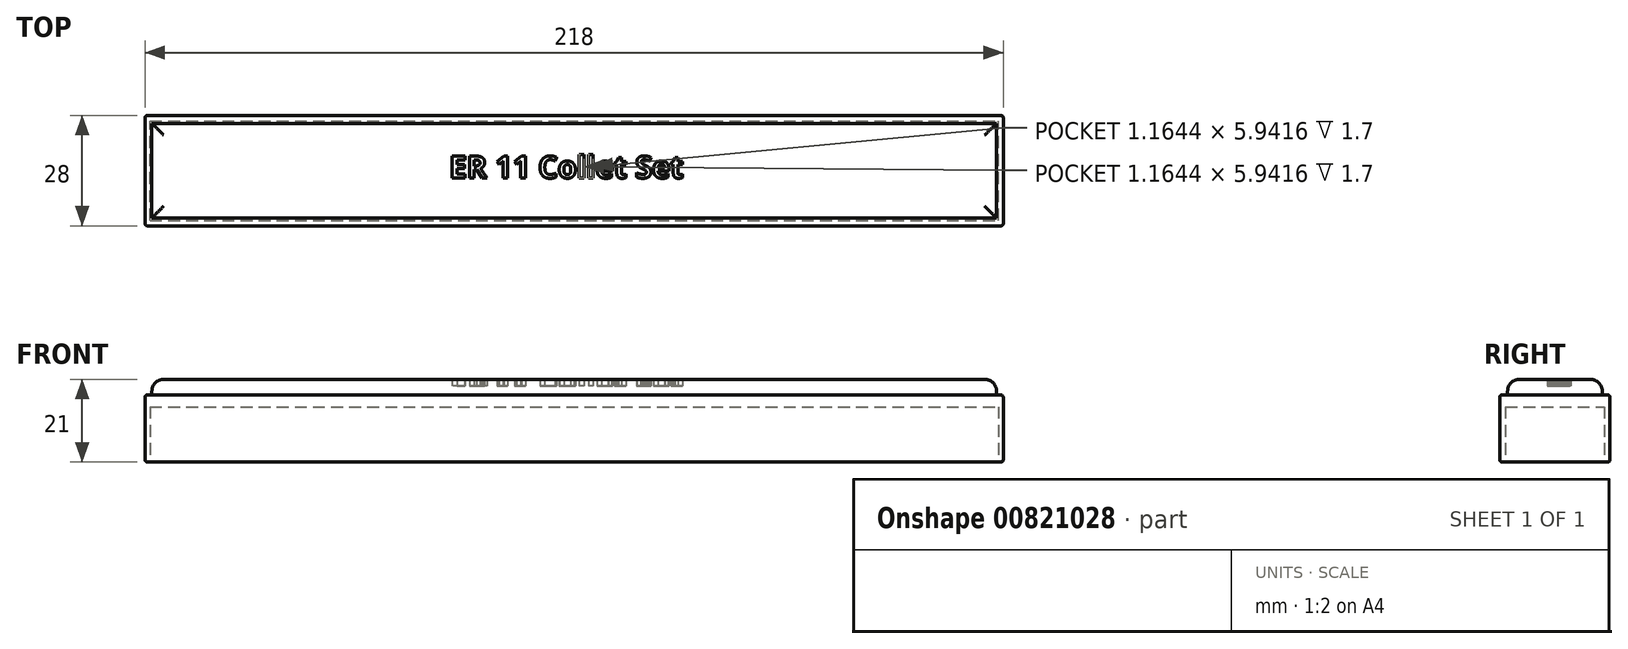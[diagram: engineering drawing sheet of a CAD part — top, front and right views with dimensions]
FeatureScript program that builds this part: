
annotation { "Feature Type Name" : "Feature", "Feature Type Description" : "" }
export const myFeature = defineFeature(function(context is Context, id is Id, definition is map)
    precondition{}
    {
        {
            var Q0;
            Q0=qCreatedBy(makeId("Top.planeOp"),FACE);
            var sketch = newSketch(context, id + "F0", { "sketchPlane" : qUnion([Q0])});
            skLineSegment(sketch, "E0.bottom", {"start": v(-109, 14) * mm, "end": v(109, 14) * mm});
            skLineSegment(sketch, "E0.top", {"start": v(-109, -14) * mm, "end": v(109, -14) * mm});
            skLineSegment(sketch, "E0.left", {"start": v(-109, 14) * mm, "end": v(-109, -14) * mm});
            skLineSegment(sketch, "E0.right", {"start": v(109, 14) * mm, "end": v(109, -14) * mm});
            skPoint(sketch, "E0.middle", {"position": v(0, 0) * mm});
            skLineSegment(sketch, "E1.bottom", {"start": v(-107.75, -12.6) * mm, "end": v(107.75, -12.6) * mm});
            skLineSegment(sketch, "E1.top", {"start": v(-107.75, 12.6) * mm, "end": v(107.75, 12.6) * mm});
            skLineSegment(sketch, "E1.left", {"start": v(-107.75, -12.6) * mm, "end": v(-107.75, 12.6) * mm});
            skLineSegment(sketch, "E1.right", {"start": v(107.75, -12.6) * mm, "end": v(107.75, 12.6) * mm});
            skSolve(sketch);
        }
        {
            var Q0;
            Q0 = qSketchRegion(id + "F0", true);
            extrude(context, id + "F1", {"entities" : qUnion([Q0]), "depth" : 14 * mm, "offsetDistance" : 25 * mm});
        }
        {
            var Q0;
            Q0=makeQuery(id+"F1.opExtrude","CAP_FACE",FACE,{"disambiguationData":[OSD([sQuery(id+"F0.wireOp",EDGE,"E0.bottom"),sQuery(id+"F0.wireOp",EDGE,"E0.top"),sQuery(id+"F0.wireOp",EDGE,"E0.left"),sQuery(id+"F0.wireOp",EDGE,"E0.right"),sQuery(id+"F0.wireOp",EDGE,"E1.bottom"),sQuery(id+"F0.wireOp",EDGE,"E1.top"),sQuery(id+"F0.wireOp",EDGE,"E1.left"),sQuery(id+"F0.wireOp",EDGE,"E1.right")])],"isStart":false});
            var sketch = newSketch(context, id + "F2", { "sketchPlane" : qUnion([Q0])});
            skLineSegment(sketch, "E2.bottom", {"start": v(109, -14) * mm, "end": v(-109, -14) * mm});
            skLineSegment(sketch, "E2.top", {"start": v(109, 14) * mm, "end": v(-109, 14) * mm});
            skLineSegment(sketch, "E2.left", {"start": v(109, -14) * mm, "end": v(109, 14) * mm});
            skLineSegment(sketch, "E2.right", {"start": v(-109, -14) * mm, "end": v(-109, 14) * mm});
            skPoint(sketch, "E2.middle", {"position": v(0, 0) * mm});
            skText(sketch, "E3", { "text": "ER 11 Collet Set", "fontName": "OpenSans-Bold.ttf"});
            const initialGuessF2  = {"E3": [-0.03167, 0.03052, 1, 0, 0.00563]};
            skSetInitialGuess(sketch, initialGuessF2);
            skSolve(sketch);
        }
        {
            var Q0;
            Q0 = qSketchRegion(id + "F2", true);
            extrude(context, id + "F3", {"entities" : qUnion([Q0]), "operationType" : NewBodyOperationType.ADD, "depth" : 3 * mm, "offsetDistance" : 25 * mm});
        }
        {
            var Q0;
            Q0=makeQuery(id+"F1.opExtrude","CAP_EDGE",EDGE,{"disambiguationData":[OSD([sQuery(id+"F0.wireOp",EDGE,"E0.top")])],"isStart":true});
            var Q1;
            Q1=makeQuery(id+"F1.opExtrude","CAP_EDGE",EDGE,{"disambiguationData":[OSD([sQuery(id+"F0.wireOp",EDGE,"E0.left")])],"isStart":true});
            var Q2;
            Q2=makeQuery(id+"F1.opExtrude","CAP_EDGE",EDGE,{"disambiguationData":[OSD([sQuery(id+"F0.wireOp",EDGE,"E0.right")])],"isStart":true});
            var Q3;
            Q3=makeQuery(id+"F3.boolean.opBoolean","MERGE",EDGE,{"derivedFrom":[makeQuery(id+"F1.opExtrude","SWEPT_EDGE",EDGE,{"disambiguationData":[OSD([sQuery(id+"F0.wireOp",EDGE,"E0.top"),sQuery(id+"F0.wireOp",EDGE,"E0.right")])]}),makeQuery(id+"F3.opExtrude","SWEPT_EDGE",EDGE,{"disambiguationData":[OSD([sQuery(id+"F2.wireOp",EDGE,"E2.bottom"),sQuery(id+"F2.wireOp",EDGE,"E2.left")])]})]});
            var Q4;
            Q4=makeQuery(id+"F3.opExtrude","CAP_EDGE",EDGE,{"disambiguationData":[OSD([sQuery(id+"F2.wireOp",EDGE,"E2.bottom")])],"isStart":false});
            var Q5;
            Q5=makeQuery(id+"F3.opExtrude","CAP_EDGE",EDGE,{"disambiguationData":[OSD([sQuery(id+"F2.wireOp",EDGE,"E2.left")])],"isStart":false});
            var Q6;
            Q6=makeQuery(id+"F3.opExtrude","CAP_EDGE",EDGE,{"disambiguationData":[OSD([sQuery(id+"F2.wireOp",EDGE,"E2.top")])],"isStart":false});
            var Q7;
            Q7=makeQuery(id+"F3.boolean.opBoolean","MERGE",FACE,{"derivedFrom":[makeQuery(id+"F1.opExtrude","SWEPT_FACE",FACE,{"disambiguationData":[OSD([sQuery(id+"F0.wireOp",EDGE,"E0.bottom")])]}),makeQuery(id+"F3.opExtrude","SWEPT_FACE",FACE,{"disambiguationData":[OSD([sQuery(id+"F2.wireOp",EDGE,"E2.top")])]})]});
            var Q8;
            Q8=makeQuery(id+"F1.opExtrude","CAP_EDGE",EDGE,{"disambiguationData":[OSD([sQuery(id+"F0.wireOp",EDGE,"E0.bottom")])],"isStart":true});
            var Q9;
            Q9=makeQuery(id+"F3.opExtrude","CAP_EDGE",EDGE,{"disambiguationData":[OSD([sQuery(id+"F2.wireOp",EDGE,"E2.right")])],"isStart":false});
            var Q10;
            Q10=makeQuery(id+"F3.boolean.opBoolean","MERGE",EDGE,{"derivedFrom":[makeQuery(id+"F1.opExtrude","SWEPT_EDGE",EDGE,{"disambiguationData":[OSD([sQuery(id+"F0.wireOp",EDGE,"E0.top"),sQuery(id+"F0.wireOp",EDGE,"E0.left")])]}),makeQuery(id+"F3.opExtrude","SWEPT_EDGE",EDGE,{"disambiguationData":[OSD([sQuery(id+"F2.wireOp",EDGE,"E2.bottom"),sQuery(id+"F2.wireOp",EDGE,"E2.right")])]})]});
            fillet(context, id + "F4", {"entities" : qUnion([Q0, Q1, Q2, Q3, Q4, Q5, Q6, Q7, Q8, Q9, Q10]), "radius" : .5 * mm, "tangentPropagation" : true, "allowEdgeOverflow" : false});
        }
        {
            var Q0;
            Q0=makeQuery(id+"F3.opExtrude","CAP_FACE",FACE,{"disambiguationData":[OSD([sQuery(id+"F2.wireOp",EDGE,"E2.bottom"),sQuery(id+"F2.wireOp",EDGE,"E2.top"),sQuery(id+"F2.wireOp",EDGE,"E2.left"),sQuery(id+"F2.wireOp",EDGE,"E2.right"),sQuery(id+"F2.wireOp",EDGE,"E3.sketch_text.stroke-0"),sQuery(id+"F2.wireOp",EDGE,"E3.sketch_text.stroke-1"),sQuery(id+"F2.wireOp",EDGE,"E3.sketch_text.stroke-2"),sQuery(id+"F2.wireOp",EDGE,"E3.sketch_text.stroke-3"),sQuery(id+"F2.wireOp",EDGE,"E3.sketch_text.stroke-4"),sQuery(id+"F2.wireOp",EDGE,"E3.sketch_text.stroke-5"),sQuery(id+"F2.wireOp",EDGE,"E3.sketch_text.stroke-6"),sQuery(id+"F2.wireOp",EDGE,"E3.sketch_text.stroke-7"),sQuery(id+"F2.wireOp",EDGE,"E3.sketch_text.stroke-8"),sQuery(id+"F2.wireOp",EDGE,"E3.sketch_text.stroke-9"),sQuery(id+"F2.wireOp",EDGE,"E3.sketch_text.stroke-10"),sQuery(id+"F2.wireOp",EDGE,"E3.sketch_text.stroke-11"),sQuery(id+"F2.wireOp",EDGE,"E3.sketch_text.stroke-19"),sQuery(id+"F2.wireOp",EDGE,"E3.sketch_text.stroke-20"),sQuery(id+"F2.wireOp",EDGE,"E3.sketch_text.stroke-21"),sQuery(id+"F2.wireOp",EDGE,"E3.sketch_text.stroke-22"),sQuery(id+"F2.wireOp",EDGE,"E3.sketch_text.stroke-23"),sQuery(id+"F2.wireOp",EDGE,"E3.sketch_text.stroke-24"),sQuery(id+"F2.wireOp",EDGE,"E3.sketch_text.stroke-25"),sQuery(id+"F2.wireOp",EDGE,"E3.sketch_text.stroke-26"),sQuery(id+"F2.wireOp",EDGE,"E3.sketch_text.stroke-27"),sQuery(id+"F2.wireOp",EDGE,"E3.sketch_text.stroke-28"),sQuery(id+"F2.wireOp",EDGE,"E3.sketch_text.stroke-29"),sQuery(id+"F2.wireOp",EDGE,"E3.sketch_text.stroke-30"),sQuery(id+"F2.wireOp",EDGE,"E3.sketch_text.stroke-31"),sQuery(id+"F2.wireOp",EDGE,"E3.sketch_text.stroke-32"),sQuery(id+"F2.wireOp",EDGE,"E3.sketch_text.stroke-33"),sQuery(id+"F2.wireOp",EDGE,"E3.sketch_text.stroke-34"),sQuery(id+"F2.wireOp",EDGE,"E3.sketch_text.stroke-35"),sQuery(id+"F2.wireOp",EDGE,"E3.sketch_text.stroke-36"),sQuery(id+"F2.wireOp",EDGE,"E3.sketch_text.stroke-37"),sQuery(id+"F2.wireOp",EDGE,"E3.sketch_text.stroke-38"),sQuery(id+"F2.wireOp",EDGE,"E3.sketch_text.stroke-39"),sQuery(id+"F2.wireOp",EDGE,"E3.sketch_text.stroke-40"),sQuery(id+"F2.wireOp",EDGE,"E3.sketch_text.stroke-41"),sQuery(id+"F2.wireOp",EDGE,"E3.sketch_text.stroke-42"),sQuery(id+"F2.wireOp",EDGE,"E3.sketch_text.stroke-43"),sQuery(id+"F2.wireOp",EDGE,"E3.sketch_text.stroke-44"),sQuery(id+"F2.wireOp",EDGE,"E3.sketch_text.stroke-45"),sQuery(id+"F2.wireOp",EDGE,"E3.sketch_text.stroke-46"),sQuery(id+"F2.wireOp",EDGE,"E3.sketch_text.stroke-47"),sQuery(id+"F2.wireOp",EDGE,"E3.sketch_text.stroke-48"),sQuery(id+"F2.wireOp",EDGE,"E3.sketch_text.stroke-49"),sQuery(id+"F2.wireOp",EDGE,"E3.sketch_text.stroke-50"),sQuery(id+"F2.wireOp",EDGE,"E3.sketch_text.stroke-51"),sQuery(id+"F2.wireOp",EDGE,"E3.sketch_text.stroke-52"),sQuery(id+"F2.wireOp",EDGE,"E3.sketch_text.stroke-53"),sQuery(id+"F2.wireOp",EDGE,"E3.sketch_text.stroke-54"),sQuery(id+"F2.wireOp",EDGE,"E3.sketch_text.stroke-55"),sQuery(id+"F2.wireOp",EDGE,"E3.sketch_text.stroke-56"),sQuery(id+"F2.wireOp",EDGE,"E3.sketch_text.stroke-57"),sQuery(id+"F2.wireOp",EDGE,"E3.sketch_text.stroke-58"),sQuery(id+"F2.wireOp",EDGE,"E3.sketch_text.stroke-59"),sQuery(id+"F2.wireOp",EDGE,"E3.sketch_text.stroke-60"),sQuery(id+"F2.wireOp",EDGE,"E3.sketch_text.stroke-61"),sQuery(id+"F2.wireOp",EDGE,"E3.sketch_text.stroke-62"),sQuery(id+"F2.wireOp",EDGE,"E3.sketch_text.stroke-63"),sQuery(id+"F2.wireOp",EDGE,"E3.sketch_text.stroke-64"),sQuery(id+"F2.wireOp",EDGE,"E3.sketch_text.stroke-65"),sQuery(id+"F2.wireOp",EDGE,"E3.sketch_text.stroke-74"),sQuery(id+"F2.wireOp",EDGE,"E3.sketch_text.stroke-75"),sQuery(id+"F2.wireOp",EDGE,"E3.sketch_text.stroke-76"),sQuery(id+"F2.wireOp",EDGE,"E3.sketch_text.stroke-77"),sQuery(id+"F2.wireOp",EDGE,"E3.sketch_text.stroke-78"),sQuery(id+"F2.wireOp",EDGE,"E3.sketch_text.stroke-79"),sQuery(id+"F2.wireOp",EDGE,"E3.sketch_text.stroke-80"),sQuery(id+"F2.wireOp",EDGE,"E3.sketch_text.stroke-81"),sQuery(id+"F2.wireOp",EDGE,"E3.sketch_text.stroke-82"),sQuery(id+"F2.wireOp",EDGE,"E3.sketch_text.stroke-83"),sQuery(id+"F2.wireOp",EDGE,"E3.sketch_text.stroke-84"),sQuery(id+"F2.wireOp",EDGE,"E3.sketch_text.stroke-85"),sQuery(id+"F2.wireOp",EDGE,"E3.sketch_text.stroke-86"),sQuery(id+"F2.wireOp",EDGE,"E3.sketch_text.stroke-87"),sQuery(id+"F2.wireOp",EDGE,"E3.sketch_text.stroke-88"),sQuery(id+"F2.wireOp",EDGE,"E3.sketch_text.stroke-89"),sQuery(id+"F2.wireOp",EDGE,"E3.sketch_text.stroke-90"),sQuery(id+"F2.wireOp",EDGE,"E3.sketch_text.stroke-91"),sQuery(id+"F2.wireOp",EDGE,"E3.sketch_text.stroke-97"),sQuery(id+"F2.wireOp",EDGE,"E3.sketch_text.stroke-98"),sQuery(id+"F2.wireOp",EDGE,"E3.sketch_text.stroke-99"),sQuery(id+"F2.wireOp",EDGE,"E3.sketch_text.stroke-100"),sQuery(id+"F2.wireOp",EDGE,"E3.sketch_text.stroke-101"),sQuery(id+"F2.wireOp",EDGE,"E3.sketch_text.stroke-102"),sQuery(id+"F2.wireOp",EDGE,"E3.sketch_text.stroke-103"),sQuery(id+"F2.wireOp",EDGE,"E3.sketch_text.stroke-104"),sQuery(id+"F2.wireOp",EDGE,"E3.sketch_text.stroke-105"),sQuery(id+"F2.wireOp",EDGE,"E3.sketch_text.stroke-106"),sQuery(id+"F2.wireOp",EDGE,"E3.sketch_text.stroke-107"),sQuery(id+"F2.wireOp",EDGE,"E3.sketch_text.stroke-108"),sQuery(id+"F2.wireOp",EDGE,"E3.sketch_text.stroke-109"),sQuery(id+"F2.wireOp",EDGE,"E3.sketch_text.stroke-110"),sQuery(id+"F2.wireOp",EDGE,"E3.sketch_text.stroke-111"),sQuery(id+"F2.wireOp",EDGE,"E3.sketch_text.stroke-112"),sQuery(id+"F2.wireOp",EDGE,"E3.sketch_text.stroke-113"),sQuery(id+"F2.wireOp",EDGE,"E3.sketch_text.stroke-114"),sQuery(id+"F2.wireOp",EDGE,"E3.sketch_text.stroke-115"),sQuery(id+"F2.wireOp",EDGE,"E3.sketch_text.stroke-116"),sQuery(id+"F2.wireOp",EDGE,"E3.sketch_text.stroke-117"),sQuery(id+"F2.wireOp",EDGE,"E3.sketch_text.stroke-118"),sQuery(id+"F2.wireOp",EDGE,"E3.sketch_text.stroke-119"),sQuery(id+"F2.wireOp",EDGE,"E3.sketch_text.stroke-120"),sQuery(id+"F2.wireOp",EDGE,"E3.sketch_text.stroke-121"),sQuery(id+"F2.wireOp",EDGE,"E3.sketch_text.stroke-122"),sQuery(id+"F2.wireOp",EDGE,"E3.sketch_text.stroke-123"),sQuery(id+"F2.wireOp",EDGE,"E3.sketch_text.stroke-124"),sQuery(id+"F2.wireOp",EDGE,"E3.sketch_text.stroke-125"),sQuery(id+"F2.wireOp",EDGE,"E3.sketch_text.stroke-126"),sQuery(id+"F2.wireOp",EDGE,"E3.sketch_text.stroke-127"),sQuery(id+"F2.wireOp",EDGE,"E3.sketch_text.stroke-128"),sQuery(id+"F2.wireOp",EDGE,"E3.sketch_text.stroke-129"),sQuery(id+"F2.wireOp",EDGE,"E3.sketch_text.stroke-130"),sQuery(id+"F2.wireOp",EDGE,"E3.sketch_text.stroke-131"),sQuery(id+"F2.wireOp",EDGE,"E3.sketch_text.stroke-132"),sQuery(id+"F2.wireOp",EDGE,"E3.sketch_text.stroke-133"),sQuery(id+"F2.wireOp",EDGE,"E3.sketch_text.stroke-134"),sQuery(id+"F2.wireOp",EDGE,"E3.sketch_text.stroke-135"),sQuery(id+"F2.wireOp",EDGE,"E3.sketch_text.stroke-136"),sQuery(id+"F2.wireOp",EDGE,"E3.sketch_text.stroke-137"),sQuery(id+"F2.wireOp",EDGE,"E3.sketch_text.stroke-138"),sQuery(id+"F2.wireOp",EDGE,"E3.sketch_text.stroke-139"),sQuery(id+"F2.wireOp",EDGE,"E3.sketch_text.stroke-140"),sQuery(id+"F2.wireOp",EDGE,"E3.sketch_text.stroke-141"),sQuery(id+"F2.wireOp",EDGE,"E3.sketch_text.stroke-142"),sQuery(id+"F2.wireOp",EDGE,"E3.sketch_text.stroke-143"),sQuery(id+"F2.wireOp",EDGE,"E3.sketch_text.stroke-144"),sQuery(id+"F2.wireOp",EDGE,"E3.sketch_text.stroke-145"),sQuery(id+"F2.wireOp",EDGE,"E3.sketch_text.stroke-146"),sQuery(id+"F2.wireOp",EDGE,"E3.sketch_text.stroke-147"),sQuery(id+"F2.wireOp",EDGE,"E3.sketch_text.stroke-148"),sQuery(id+"F2.wireOp",EDGE,"E3.sketch_text.stroke-149"),sQuery(id+"F2.wireOp",EDGE,"E3.sketch_text.stroke-150"),sQuery(id+"F2.wireOp",EDGE,"E3.sketch_text.stroke-151"),sQuery(id+"F2.wireOp",EDGE,"E3.sketch_text.stroke-152"),sQuery(id+"F2.wireOp",EDGE,"E3.sketch_text.stroke-153"),sQuery(id+"F2.wireOp",EDGE,"E3.sketch_text.stroke-154"),sQuery(id+"F2.wireOp",EDGE,"E3.sketch_text.stroke-155"),sQuery(id+"F2.wireOp",EDGE,"E3.sketch_text.stroke-156"),sQuery(id+"F2.wireOp",EDGE,"E3.sketch_text.stroke-157"),sQuery(id+"F2.wireOp",EDGE,"E3.sketch_text.stroke-163"),sQuery(id+"F2.wireOp",EDGE,"E3.sketch_text.stroke-164"),sQuery(id+"F2.wireOp",EDGE,"E3.sketch_text.stroke-165"),sQuery(id+"F2.wireOp",EDGE,"E3.sketch_text.stroke-166"),sQuery(id+"F2.wireOp",EDGE,"E3.sketch_text.stroke-167"),sQuery(id+"F2.wireOp",EDGE,"E3.sketch_text.stroke-168"),sQuery(id+"F2.wireOp",EDGE,"E3.sketch_text.stroke-169"),sQuery(id+"F2.wireOp",EDGE,"E3.sketch_text.stroke-170"),sQuery(id+"F2.wireOp",EDGE,"E3.sketch_text.stroke-171"),sQuery(id+"F2.wireOp",EDGE,"E3.sketch_text.stroke-172"),sQuery(id+"F2.wireOp",EDGE,"E3.sketch_text.stroke-173"),sQuery(id+"F2.wireOp",EDGE,"E3.sketch_text.stroke-174"),sQuery(id+"F2.wireOp",EDGE,"E3.sketch_text.stroke-175"),sQuery(id+"F2.wireOp",EDGE,"E3.sketch_text.stroke-176"),sQuery(id+"F2.wireOp",EDGE,"E3.sketch_text.stroke-177"),sQuery(id+"F2.wireOp",EDGE,"E3.sketch_text.stroke-178"),sQuery(id+"F2.wireOp",EDGE,"E3.sketch_text.stroke-179"),sQuery(id+"F2.wireOp",EDGE,"E3.sketch_text.stroke-180"),sQuery(id+"F2.wireOp",EDGE,"E3.sketch_text.stroke-181"),sQuery(id+"F2.wireOp",EDGE,"E3.sketch_text.stroke-182"),sQuery(id+"F2.wireOp",EDGE,"E3.sketch_text.stroke-183"),sQuery(id+"F2.wireOp",EDGE,"E3.sketch_text.stroke-184"),sQuery(id+"F2.wireOp",EDGE,"E3.sketch_text.stroke-185"),sQuery(id+"F2.wireOp",EDGE,"E3.sketch_text.stroke-186"),sQuery(id+"F2.wireOp",EDGE,"E3.sketch_text.stroke-187"),sQuery(id+"F2.wireOp",EDGE,"E3.sketch_text.stroke-188"),sQuery(id+"F2.wireOp",EDGE,"E3.sketch_text.stroke-189"),sQuery(id+"F2.wireOp",EDGE,"E3.sketch_text.stroke-190"),sQuery(id+"F2.wireOp",EDGE,"E3.sketch_text.stroke-191"),sQuery(id+"F2.wireOp",EDGE,"E3.sketch_text.stroke-192"),sQuery(id+"F2.wireOp",EDGE,"E3.sketch_text.stroke-193"),sQuery(id+"F2.wireOp",EDGE,"E3.sketch_text.stroke-194"),sQuery(id+"F2.wireOp",EDGE,"E3.sketch_text.stroke-195")])],"isStart":false});
            var sketch = newSketch(context, id + "F5", { "sketchPlane" : qUnion([Q0])});
            skLineSegment(sketch, "E4.bottom", {"start": v(-107.3, 12.02) * mm, "end": v(107.3, 12.02) * mm});
            skLineSegment(sketch, "E4.top", {"start": v(-107.3, -12.02) * mm, "end": v(107.3, -12.02) * mm});
            skLineSegment(sketch, "E4.left", {"start": v(-107.3, 12.02) * mm, "end": v(-107.3, -12.02) * mm});
            skLineSegment(sketch, "E4.right", {"start": v(107.3, 12.02) * mm, "end": v(107.3, -12.02) * mm});
            skPoint(sketch, "E4.middle", {"position": v(0, 0) * mm});
            skSolve(sketch);
        }
        {
            var Q0;
            Q0 = qSketchRegion(id + "F5", true);
            extrude(context, id + "F6", {"entities" : qUnion([Q0]), "operationType" : NewBodyOperationType.ADD, "depth" : 4 * mm, "offsetDistance" : 25 * mm});
        }
        {
            var Q0;
            Q0=makeQuery(id+"F6.opExtrude","CAP_EDGE",EDGE,{"disambiguationData":[OSD([sQuery(id+"F5.wireOp",EDGE,"E4.top")])],"isStart":false});
            var Q1;
            Q1=makeQuery(id+"F6.opExtrude","CAP_EDGE",EDGE,{"disambiguationData":[OSD([sQuery(id+"F5.wireOp",EDGE,"E4.bottom")])],"isStart":false});
            var Q2;
            Q2=makeQuery(id+"F6.opExtrude","CAP_EDGE",EDGE,{"disambiguationData":[OSD([sQuery(id+"F5.wireOp",EDGE,"E4.left")])],"isStart":false});
            var Q3;
            Q3=makeQuery(id+"F6.opExtrude","CAP_EDGE",EDGE,{"disambiguationData":[OSD([sQuery(id+"F5.wireOp",EDGE,"E4.right")])],"isStart":false});
            fillet(context, id + "F7", {"entities" : qUnion([Q0, Q1, Q2, Q3]), "radius" : 3 * mm, "tangentPropagation" : true, "allowEdgeOverflow" : false});
        }
        {
            var Q0;
            Q0=makeQuery(id+"F3.opExtrude","SWEPT_BODY",BODY,{"disambiguationData":[OSD([sQuery(id+"F2.wireOp",EDGE,"E3.sketch_text.stroke-158"),sQuery(id+"F2.wireOp",EDGE,"E3.sketch_text.stroke-159"),sQuery(id+"F2.wireOp",EDGE,"E3.sketch_text.stroke-160"),sQuery(id+"F2.wireOp",EDGE,"E3.sketch_text.stroke-161"),sQuery(id+"F2.wireOp",EDGE,"E3.sketch_text.stroke-162"),sQuery(id+"F2.wireOp",EDGE,"E3.sketch_text.stroke-163"),sQuery(id+"F2.wireOp",EDGE,"E3.sketch_text.stroke-164"),sQuery(id+"F2.wireOp",EDGE,"E3.sketch_text.stroke-165"),sQuery(id+"F2.wireOp",EDGE,"E3.sketch_text.stroke-166"),sQuery(id+"F2.wireOp",EDGE,"E3.sketch_text.stroke-167"),sQuery(id+"F2.wireOp",EDGE,"E3.sketch_text.stroke-168"),sQuery(id+"F2.wireOp",EDGE,"E3.sketch_text.stroke-169"),sQuery(id+"F2.wireOp",EDGE,"E3.sketch_text.stroke-170"),sQuery(id+"F2.wireOp",EDGE,"E3.sketch_text.stroke-171"),sQuery(id+"F2.wireOp",EDGE,"E3.sketch_text.stroke-172"),sQuery(id+"F2.wireOp",EDGE,"E3.sketch_text.stroke-173"),sQuery(id+"F2.wireOp",EDGE,"E3.sketch_text.stroke-174"),sQuery(id+"F2.wireOp",EDGE,"E3.sketch_text.stroke-175"),sQuery(id+"F2.wireOp",EDGE,"E3.sketch_text.stroke-176"),sQuery(id+"F2.wireOp",EDGE,"E3.sketch_text.stroke-177")])]});
            var Q1;
            Q1=makeQuery(id+"F3.opExtrude","SWEPT_BODY",BODY,{"disambiguationData":[OSD([sQuery(id+"F2.wireOp",EDGE,"E3.sketch_text.stroke-0"),sQuery(id+"F2.wireOp",EDGE,"E3.sketch_text.stroke-1"),sQuery(id+"F2.wireOp",EDGE,"E3.sketch_text.stroke-2"),sQuery(id+"F2.wireOp",EDGE,"E3.sketch_text.stroke-3"),sQuery(id+"F2.wireOp",EDGE,"E3.sketch_text.stroke-4"),sQuery(id+"F2.wireOp",EDGE,"E3.sketch_text.stroke-5"),sQuery(id+"F2.wireOp",EDGE,"E3.sketch_text.stroke-6"),sQuery(id+"F2.wireOp",EDGE,"E3.sketch_text.stroke-7"),sQuery(id+"F2.wireOp",EDGE,"E3.sketch_text.stroke-8"),sQuery(id+"F2.wireOp",EDGE,"E3.sketch_text.stroke-9"),sQuery(id+"F2.wireOp",EDGE,"E3.sketch_text.stroke-10"),sQuery(id+"F2.wireOp",EDGE,"E3.sketch_text.stroke-11")])]});
            var Q2;
            Q2=makeQuery(id+"F3.opExtrude","SWEPT_BODY",BODY,{"disambiguationData":[OSD([sQuery(id+"F2.wireOp",EDGE,"E3.sketch_text.stroke-12"),sQuery(id+"F2.wireOp",EDGE,"E3.sketch_text.stroke-13"),sQuery(id+"F2.wireOp",EDGE,"E3.sketch_text.stroke-14"),sQuery(id+"F2.wireOp",EDGE,"E3.sketch_text.stroke-15"),sQuery(id+"F2.wireOp",EDGE,"E3.sketch_text.stroke-16"),sQuery(id+"F2.wireOp",EDGE,"E3.sketch_text.stroke-17"),sQuery(id+"F2.wireOp",EDGE,"E3.sketch_text.stroke-18"),sQuery(id+"F2.wireOp",EDGE,"E3.sketch_text.stroke-19"),sQuery(id+"F2.wireOp",EDGE,"E3.sketch_text.stroke-20"),sQuery(id+"F2.wireOp",EDGE,"E3.sketch_text.stroke-21"),sQuery(id+"F2.wireOp",EDGE,"E3.sketch_text.stroke-22"),sQuery(id+"F2.wireOp",EDGE,"E3.sketch_text.stroke-23"),sQuery(id+"F2.wireOp",EDGE,"E3.sketch_text.stroke-24"),sQuery(id+"F2.wireOp",EDGE,"E3.sketch_text.stroke-25"),sQuery(id+"F2.wireOp",EDGE,"E3.sketch_text.stroke-26"),sQuery(id+"F2.wireOp",EDGE,"E3.sketch_text.stroke-27"),sQuery(id+"F2.wireOp",EDGE,"E3.sketch_text.stroke-28"),sQuery(id+"F2.wireOp",EDGE,"E3.sketch_text.stroke-29"),sQuery(id+"F2.wireOp",EDGE,"E3.sketch_text.stroke-30")])]});
            var Q3;
            Q3=makeQuery(id+"F3.opExtrude","SWEPT_BODY",BODY,{"disambiguationData":[OSD([sQuery(id+"F2.wireOp",EDGE,"E3.sketch_text.stroke-41"),sQuery(id+"F2.wireOp",EDGE,"E3.sketch_text.stroke-42"),sQuery(id+"F2.wireOp",EDGE,"E3.sketch_text.stroke-43"),sQuery(id+"F2.wireOp",EDGE,"E3.sketch_text.stroke-44"),sQuery(id+"F2.wireOp",EDGE,"E3.sketch_text.stroke-45"),sQuery(id+"F2.wireOp",EDGE,"E3.sketch_text.stroke-46"),sQuery(id+"F2.wireOp",EDGE,"E3.sketch_text.stroke-47"),sQuery(id+"F2.wireOp",EDGE,"E3.sketch_text.stroke-48"),sQuery(id+"F2.wireOp",EDGE,"E3.sketch_text.stroke-49"),sQuery(id+"F2.wireOp",EDGE,"E3.sketch_text.stroke-50")])]});
            var Q4;
            Q4=makeQuery(id+"F3.opExtrude","SWEPT_BODY",BODY,{"disambiguationData":[OSD([sQuery(id+"F2.wireOp",EDGE,"E3.sketch_text.stroke-31"),sQuery(id+"F2.wireOp",EDGE,"E3.sketch_text.stroke-32"),sQuery(id+"F2.wireOp",EDGE,"E3.sketch_text.stroke-33"),sQuery(id+"F2.wireOp",EDGE,"E3.sketch_text.stroke-34"),sQuery(id+"F2.wireOp",EDGE,"E3.sketch_text.stroke-35"),sQuery(id+"F2.wireOp",EDGE,"E3.sketch_text.stroke-36"),sQuery(id+"F2.wireOp",EDGE,"E3.sketch_text.stroke-37"),sQuery(id+"F2.wireOp",EDGE,"E3.sketch_text.stroke-38"),sQuery(id+"F2.wireOp",EDGE,"E3.sketch_text.stroke-39"),sQuery(id+"F2.wireOp",EDGE,"E3.sketch_text.stroke-40")])]});
            var Q5;
            Q5=makeQuery(id+"F3.opExtrude","SWEPT_BODY",BODY,{"disambiguationData":[OSD([sQuery(id+"F2.wireOp",EDGE,"E3.sketch_text.stroke-66"),sQuery(id+"F2.wireOp",EDGE,"E3.sketch_text.stroke-67"),sQuery(id+"F2.wireOp",EDGE,"E3.sketch_text.stroke-68"),sQuery(id+"F2.wireOp",EDGE,"E3.sketch_text.stroke-69"),sQuery(id+"F2.wireOp",EDGE,"E3.sketch_text.stroke-70"),sQuery(id+"F2.wireOp",EDGE,"E3.sketch_text.stroke-71"),sQuery(id+"F2.wireOp",EDGE,"E3.sketch_text.stroke-72"),sQuery(id+"F2.wireOp",EDGE,"E3.sketch_text.stroke-73"),sQuery(id+"F2.wireOp",EDGE,"E3.sketch_text.stroke-74"),sQuery(id+"F2.wireOp",EDGE,"E3.sketch_text.stroke-75"),sQuery(id+"F2.wireOp",EDGE,"E3.sketch_text.stroke-76"),sQuery(id+"F2.wireOp",EDGE,"E3.sketch_text.stroke-77"),sQuery(id+"F2.wireOp",EDGE,"E3.sketch_text.stroke-78"),sQuery(id+"F2.wireOp",EDGE,"E3.sketch_text.stroke-79"),sQuery(id+"F2.wireOp",EDGE,"E3.sketch_text.stroke-80"),sQuery(id+"F2.wireOp",EDGE,"E3.sketch_text.stroke-81"),sQuery(id+"F2.wireOp",EDGE,"E3.sketch_text.stroke-82"),sQuery(id+"F2.wireOp",EDGE,"E3.sketch_text.stroke-83")])]});
            var Q6;
            Q6=makeQuery(id+"F3.opExtrude","SWEPT_BODY",BODY,{"disambiguationData":[OSD([sQuery(id+"F2.wireOp",EDGE,"E3.sketch_text.stroke-51"),sQuery(id+"F2.wireOp",EDGE,"E3.sketch_text.stroke-52"),sQuery(id+"F2.wireOp",EDGE,"E3.sketch_text.stroke-53"),sQuery(id+"F2.wireOp",EDGE,"E3.sketch_text.stroke-54"),sQuery(id+"F2.wireOp",EDGE,"E3.sketch_text.stroke-55"),sQuery(id+"F2.wireOp",EDGE,"E3.sketch_text.stroke-56"),sQuery(id+"F2.wireOp",EDGE,"E3.sketch_text.stroke-57"),sQuery(id+"F2.wireOp",EDGE,"E3.sketch_text.stroke-58"),sQuery(id+"F2.wireOp",EDGE,"E3.sketch_text.stroke-59"),sQuery(id+"F2.wireOp",EDGE,"E3.sketch_text.stroke-60"),sQuery(id+"F2.wireOp",EDGE,"E3.sketch_text.stroke-61"),sQuery(id+"F2.wireOp",EDGE,"E3.sketch_text.stroke-62"),sQuery(id+"F2.wireOp",EDGE,"E3.sketch_text.stroke-63"),sQuery(id+"F2.wireOp",EDGE,"E3.sketch_text.stroke-64"),sQuery(id+"F2.wireOp",EDGE,"E3.sketch_text.stroke-65")])]});
            var Q7;
            Q7=makeQuery(id+"F3.opExtrude","SWEPT_BODY",BODY,{"disambiguationData":[OSD([sQuery(id+"F2.wireOp",EDGE,"E3.sketch_text.stroke-84"),sQuery(id+"F2.wireOp",EDGE,"E3.sketch_text.stroke-85"),sQuery(id+"F2.wireOp",EDGE,"E3.sketch_text.stroke-86"),sQuery(id+"F2.wireOp",EDGE,"E3.sketch_text.stroke-87")])]});
            var Q8;
            Q8=makeQuery(id+"F3.opExtrude","SWEPT_BODY",BODY,{"disambiguationData":[OSD([sQuery(id+"F2.wireOp",EDGE,"E3.sketch_text.stroke-88"),sQuery(id+"F2.wireOp",EDGE,"E3.sketch_text.stroke-89"),sQuery(id+"F2.wireOp",EDGE,"E3.sketch_text.stroke-90"),sQuery(id+"F2.wireOp",EDGE,"E3.sketch_text.stroke-91")])]});
            var Q9;
            Q9=makeQuery(id+"F3.opExtrude","SWEPT_BODY",BODY,{"disambiguationData":[OSD([sQuery(id+"F2.wireOp",EDGE,"E3.sketch_text.stroke-92"),sQuery(id+"F2.wireOp",EDGE,"E3.sketch_text.stroke-93"),sQuery(id+"F2.wireOp",EDGE,"E3.sketch_text.stroke-94"),sQuery(id+"F2.wireOp",EDGE,"E3.sketch_text.stroke-95"),sQuery(id+"F2.wireOp",EDGE,"E3.sketch_text.stroke-96"),sQuery(id+"F2.wireOp",EDGE,"E3.sketch_text.stroke-97"),sQuery(id+"F2.wireOp",EDGE,"E3.sketch_text.stroke-98"),sQuery(id+"F2.wireOp",EDGE,"E3.sketch_text.stroke-99"),sQuery(id+"F2.wireOp",EDGE,"E3.sketch_text.stroke-100"),sQuery(id+"F2.wireOp",EDGE,"E3.sketch_text.stroke-101"),sQuery(id+"F2.wireOp",EDGE,"E3.sketch_text.stroke-102"),sQuery(id+"F2.wireOp",EDGE,"E3.sketch_text.stroke-103"),sQuery(id+"F2.wireOp",EDGE,"E3.sketch_text.stroke-104"),sQuery(id+"F2.wireOp",EDGE,"E3.sketch_text.stroke-105"),sQuery(id+"F2.wireOp",EDGE,"E3.sketch_text.stroke-106"),sQuery(id+"F2.wireOp",EDGE,"E3.sketch_text.stroke-107"),sQuery(id+"F2.wireOp",EDGE,"E3.sketch_text.stroke-108"),sQuery(id+"F2.wireOp",EDGE,"E3.sketch_text.stroke-109"),sQuery(id+"F2.wireOp",EDGE,"E3.sketch_text.stroke-110"),sQuery(id+"F2.wireOp",EDGE,"E3.sketch_text.stroke-111")])]});
            var Q10;
            Q10=makeQuery(id+"F3.opExtrude","SWEPT_BODY",BODY,{"disambiguationData":[OSD([sQuery(id+"F2.wireOp",EDGE,"E3.sketch_text.stroke-112"),sQuery(id+"F2.wireOp",EDGE,"E3.sketch_text.stroke-113"),sQuery(id+"F2.wireOp",EDGE,"E3.sketch_text.stroke-114"),sQuery(id+"F2.wireOp",EDGE,"E3.sketch_text.stroke-115"),sQuery(id+"F2.wireOp",EDGE,"E3.sketch_text.stroke-116"),sQuery(id+"F2.wireOp",EDGE,"E3.sketch_text.stroke-117"),sQuery(id+"F2.wireOp",EDGE,"E3.sketch_text.stroke-118"),sQuery(id+"F2.wireOp",EDGE,"E3.sketch_text.stroke-119"),sQuery(id+"F2.wireOp",EDGE,"E3.sketch_text.stroke-120"),sQuery(id+"F2.wireOp",EDGE,"E3.sketch_text.stroke-121"),sQuery(id+"F2.wireOp",EDGE,"E3.sketch_text.stroke-122"),sQuery(id+"F2.wireOp",EDGE,"E3.sketch_text.stroke-123"),sQuery(id+"F2.wireOp",EDGE,"E3.sketch_text.stroke-124"),sQuery(id+"F2.wireOp",EDGE,"E3.sketch_text.stroke-125"),sQuery(id+"F2.wireOp",EDGE,"E3.sketch_text.stroke-126"),sQuery(id+"F2.wireOp",EDGE,"E3.sketch_text.stroke-127"),sQuery(id+"F2.wireOp",EDGE,"E3.sketch_text.stroke-128"),sQuery(id+"F2.wireOp",EDGE,"E3.sketch_text.stroke-129")])]});
            var Q11;
            Q11=makeQuery(id+"F3.opExtrude","SWEPT_BODY",BODY,{"disambiguationData":[OSD([sQuery(id+"F2.wireOp",EDGE,"E3.sketch_text.stroke-130"),sQuery(id+"F2.wireOp",EDGE,"E3.sketch_text.stroke-131"),sQuery(id+"F2.wireOp",EDGE,"E3.sketch_text.stroke-132"),sQuery(id+"F2.wireOp",EDGE,"E3.sketch_text.stroke-133"),sQuery(id+"F2.wireOp",EDGE,"E3.sketch_text.stroke-134"),sQuery(id+"F2.wireOp",EDGE,"E3.sketch_text.stroke-135"),sQuery(id+"F2.wireOp",EDGE,"E3.sketch_text.stroke-136"),sQuery(id+"F2.wireOp",EDGE,"E3.sketch_text.stroke-137"),sQuery(id+"F2.wireOp",EDGE,"E3.sketch_text.stroke-138"),sQuery(id+"F2.wireOp",EDGE,"E3.sketch_text.stroke-139"),sQuery(id+"F2.wireOp",EDGE,"E3.sketch_text.stroke-140"),sQuery(id+"F2.wireOp",EDGE,"E3.sketch_text.stroke-141"),sQuery(id+"F2.wireOp",EDGE,"E3.sketch_text.stroke-142"),sQuery(id+"F2.wireOp",EDGE,"E3.sketch_text.stroke-143"),sQuery(id+"F2.wireOp",EDGE,"E3.sketch_text.stroke-144"),sQuery(id+"F2.wireOp",EDGE,"E3.sketch_text.stroke-145"),sQuery(id+"F2.wireOp",EDGE,"E3.sketch_text.stroke-146"),sQuery(id+"F2.wireOp",EDGE,"E3.sketch_text.stroke-147"),sQuery(id+"F2.wireOp",EDGE,"E3.sketch_text.stroke-148"),sQuery(id+"F2.wireOp",EDGE,"E3.sketch_text.stroke-149"),sQuery(id+"F2.wireOp",EDGE,"E3.sketch_text.stroke-150"),sQuery(id+"F2.wireOp",EDGE,"E3.sketch_text.stroke-151"),sQuery(id+"F2.wireOp",EDGE,"E3.sketch_text.stroke-152"),sQuery(id+"F2.wireOp",EDGE,"E3.sketch_text.stroke-153"),sQuery(id+"F2.wireOp",EDGE,"E3.sketch_text.stroke-154"),sQuery(id+"F2.wireOp",EDGE,"E3.sketch_text.stroke-155"),sQuery(id+"F2.wireOp",EDGE,"E3.sketch_text.stroke-156"),sQuery(id+"F2.wireOp",EDGE,"E3.sketch_text.stroke-157")])]});
            var Q12;
            Q12=makeQuery(id+"F3.opExtrude","SWEPT_BODY",BODY,{"disambiguationData":[OSD([sQuery(id+"F2.wireOp",EDGE,"E3.sketch_text.stroke-178"),sQuery(id+"F2.wireOp",EDGE,"E3.sketch_text.stroke-179"),sQuery(id+"F2.wireOp",EDGE,"E3.sketch_text.stroke-180"),sQuery(id+"F2.wireOp",EDGE,"E3.sketch_text.stroke-181"),sQuery(id+"F2.wireOp",EDGE,"E3.sketch_text.stroke-182"),sQuery(id+"F2.wireOp",EDGE,"E3.sketch_text.stroke-183"),sQuery(id+"F2.wireOp",EDGE,"E3.sketch_text.stroke-184"),sQuery(id+"F2.wireOp",EDGE,"E3.sketch_text.stroke-185"),sQuery(id+"F2.wireOp",EDGE,"E3.sketch_text.stroke-186"),sQuery(id+"F2.wireOp",EDGE,"E3.sketch_text.stroke-187"),sQuery(id+"F2.wireOp",EDGE,"E3.sketch_text.stroke-188"),sQuery(id+"F2.wireOp",EDGE,"E3.sketch_text.stroke-189"),sQuery(id+"F2.wireOp",EDGE,"E3.sketch_text.stroke-190"),sQuery(id+"F2.wireOp",EDGE,"E3.sketch_text.stroke-191"),sQuery(id+"F2.wireOp",EDGE,"E3.sketch_text.stroke-192"),sQuery(id+"F2.wireOp",EDGE,"E3.sketch_text.stroke-193"),sQuery(id+"F2.wireOp",EDGE,"E3.sketch_text.stroke-194"),sQuery(id+"F2.wireOp",EDGE,"E3.sketch_text.stroke-195")])]});
            transform(context, id + "F8", {"entities" : qUnion([Q0, Q1, Q2, Q3, Q4, Q5, Q6, Q7, Q8, Q9, Q10, Q11, Q12]), "transformType" : TransformType.TRANSLATION_3D, "dx" : 0 * mm, "dy" : -32.4 * mm, "dz" : 6.6 * mm, "makeCopy" : false});
        }
        {
            var Q0;
            Q0=makeQuery(id+"F3.opExtrude","SWEPT_BODY",BODY,{"disambiguationData":[OSD([sQuery(id+"F2.wireOp",EDGE,"E3.sketch_text.stroke-0"),sQuery(id+"F2.wireOp",EDGE,"E3.sketch_text.stroke-1"),sQuery(id+"F2.wireOp",EDGE,"E3.sketch_text.stroke-2"),sQuery(id+"F2.wireOp",EDGE,"E3.sketch_text.stroke-3"),sQuery(id+"F2.wireOp",EDGE,"E3.sketch_text.stroke-4"),sQuery(id+"F2.wireOp",EDGE,"E3.sketch_text.stroke-5"),sQuery(id+"F2.wireOp",EDGE,"E3.sketch_text.stroke-6"),sQuery(id+"F2.wireOp",EDGE,"E3.sketch_text.stroke-7"),sQuery(id+"F2.wireOp",EDGE,"E3.sketch_text.stroke-8"),sQuery(id+"F2.wireOp",EDGE,"E3.sketch_text.stroke-9"),sQuery(id+"F2.wireOp",EDGE,"E3.sketch_text.stroke-10"),sQuery(id+"F2.wireOp",EDGE,"E3.sketch_text.stroke-11")])]});
            var Q1;
            Q1=makeQuery(id+"F3.opExtrude","SWEPT_BODY",BODY,{"disambiguationData":[OSD([sQuery(id+"F2.wireOp",EDGE,"E3.sketch_text.stroke-12"),sQuery(id+"F2.wireOp",EDGE,"E3.sketch_text.stroke-13"),sQuery(id+"F2.wireOp",EDGE,"E3.sketch_text.stroke-14"),sQuery(id+"F2.wireOp",EDGE,"E3.sketch_text.stroke-15"),sQuery(id+"F2.wireOp",EDGE,"E3.sketch_text.stroke-16"),sQuery(id+"F2.wireOp",EDGE,"E3.sketch_text.stroke-17"),sQuery(id+"F2.wireOp",EDGE,"E3.sketch_text.stroke-18"),sQuery(id+"F2.wireOp",EDGE,"E3.sketch_text.stroke-19"),sQuery(id+"F2.wireOp",EDGE,"E3.sketch_text.stroke-20"),sQuery(id+"F2.wireOp",EDGE,"E3.sketch_text.stroke-21"),sQuery(id+"F2.wireOp",EDGE,"E3.sketch_text.stroke-22"),sQuery(id+"F2.wireOp",EDGE,"E3.sketch_text.stroke-23"),sQuery(id+"F2.wireOp",EDGE,"E3.sketch_text.stroke-24"),sQuery(id+"F2.wireOp",EDGE,"E3.sketch_text.stroke-25"),sQuery(id+"F2.wireOp",EDGE,"E3.sketch_text.stroke-26"),sQuery(id+"F2.wireOp",EDGE,"E3.sketch_text.stroke-27"),sQuery(id+"F2.wireOp",EDGE,"E3.sketch_text.stroke-28"),sQuery(id+"F2.wireOp",EDGE,"E3.sketch_text.stroke-29"),sQuery(id+"F2.wireOp",EDGE,"E3.sketch_text.stroke-30")])]});
            var Q2;
            Q2=makeQuery(id+"F3.opExtrude","SWEPT_BODY",BODY,{"disambiguationData":[OSD([sQuery(id+"F2.wireOp",EDGE,"E3.sketch_text.stroke-41"),sQuery(id+"F2.wireOp",EDGE,"E3.sketch_text.stroke-42"),sQuery(id+"F2.wireOp",EDGE,"E3.sketch_text.stroke-43"),sQuery(id+"F2.wireOp",EDGE,"E3.sketch_text.stroke-44"),sQuery(id+"F2.wireOp",EDGE,"E3.sketch_text.stroke-45"),sQuery(id+"F2.wireOp",EDGE,"E3.sketch_text.stroke-46"),sQuery(id+"F2.wireOp",EDGE,"E3.sketch_text.stroke-47"),sQuery(id+"F2.wireOp",EDGE,"E3.sketch_text.stroke-48"),sQuery(id+"F2.wireOp",EDGE,"E3.sketch_text.stroke-49"),sQuery(id+"F2.wireOp",EDGE,"E3.sketch_text.stroke-50")])]});
            var Q3;
            Q3=makeQuery(id+"F3.opExtrude","SWEPT_BODY",BODY,{"disambiguationData":[OSD([sQuery(id+"F2.wireOp",EDGE,"E3.sketch_text.stroke-31"),sQuery(id+"F2.wireOp",EDGE,"E3.sketch_text.stroke-32"),sQuery(id+"F2.wireOp",EDGE,"E3.sketch_text.stroke-33"),sQuery(id+"F2.wireOp",EDGE,"E3.sketch_text.stroke-34"),sQuery(id+"F2.wireOp",EDGE,"E3.sketch_text.stroke-35"),sQuery(id+"F2.wireOp",EDGE,"E3.sketch_text.stroke-36"),sQuery(id+"F2.wireOp",EDGE,"E3.sketch_text.stroke-37"),sQuery(id+"F2.wireOp",EDGE,"E3.sketch_text.stroke-38"),sQuery(id+"F2.wireOp",EDGE,"E3.sketch_text.stroke-39"),sQuery(id+"F2.wireOp",EDGE,"E3.sketch_text.stroke-40")])]});
            var Q4;
            Q4=makeQuery(id+"F3.opExtrude","SWEPT_BODY",BODY,{"disambiguationData":[OSD([sQuery(id+"F2.wireOp",EDGE,"E3.sketch_text.stroke-66"),sQuery(id+"F2.wireOp",EDGE,"E3.sketch_text.stroke-67"),sQuery(id+"F2.wireOp",EDGE,"E3.sketch_text.stroke-68"),sQuery(id+"F2.wireOp",EDGE,"E3.sketch_text.stroke-69"),sQuery(id+"F2.wireOp",EDGE,"E3.sketch_text.stroke-70"),sQuery(id+"F2.wireOp",EDGE,"E3.sketch_text.stroke-71"),sQuery(id+"F2.wireOp",EDGE,"E3.sketch_text.stroke-72"),sQuery(id+"F2.wireOp",EDGE,"E3.sketch_text.stroke-73"),sQuery(id+"F2.wireOp",EDGE,"E3.sketch_text.stroke-74"),sQuery(id+"F2.wireOp",EDGE,"E3.sketch_text.stroke-75"),sQuery(id+"F2.wireOp",EDGE,"E3.sketch_text.stroke-76"),sQuery(id+"F2.wireOp",EDGE,"E3.sketch_text.stroke-77"),sQuery(id+"F2.wireOp",EDGE,"E3.sketch_text.stroke-78"),sQuery(id+"F2.wireOp",EDGE,"E3.sketch_text.stroke-79"),sQuery(id+"F2.wireOp",EDGE,"E3.sketch_text.stroke-80"),sQuery(id+"F2.wireOp",EDGE,"E3.sketch_text.stroke-81"),sQuery(id+"F2.wireOp",EDGE,"E3.sketch_text.stroke-82"),sQuery(id+"F2.wireOp",EDGE,"E3.sketch_text.stroke-83")])]});
            var Q5;
            Q5=makeQuery(id+"F3.opExtrude","SWEPT_BODY",BODY,{"disambiguationData":[OSD([sQuery(id+"F2.wireOp",EDGE,"E3.sketch_text.stroke-51"),sQuery(id+"F2.wireOp",EDGE,"E3.sketch_text.stroke-52"),sQuery(id+"F2.wireOp",EDGE,"E3.sketch_text.stroke-53"),sQuery(id+"F2.wireOp",EDGE,"E3.sketch_text.stroke-54"),sQuery(id+"F2.wireOp",EDGE,"E3.sketch_text.stroke-55"),sQuery(id+"F2.wireOp",EDGE,"E3.sketch_text.stroke-56"),sQuery(id+"F2.wireOp",EDGE,"E3.sketch_text.stroke-57"),sQuery(id+"F2.wireOp",EDGE,"E3.sketch_text.stroke-58"),sQuery(id+"F2.wireOp",EDGE,"E3.sketch_text.stroke-59"),sQuery(id+"F2.wireOp",EDGE,"E3.sketch_text.stroke-60"),sQuery(id+"F2.wireOp",EDGE,"E3.sketch_text.stroke-61"),sQuery(id+"F2.wireOp",EDGE,"E3.sketch_text.stroke-62"),sQuery(id+"F2.wireOp",EDGE,"E3.sketch_text.stroke-63"),sQuery(id+"F2.wireOp",EDGE,"E3.sketch_text.stroke-64"),sQuery(id+"F2.wireOp",EDGE,"E3.sketch_text.stroke-65")])]});
            var Q6;
            Q6=makeQuery(id+"F3.opExtrude","SWEPT_BODY",BODY,{"disambiguationData":[OSD([sQuery(id+"F2.wireOp",EDGE,"E3.sketch_text.stroke-84"),sQuery(id+"F2.wireOp",EDGE,"E3.sketch_text.stroke-85"),sQuery(id+"F2.wireOp",EDGE,"E3.sketch_text.stroke-86"),sQuery(id+"F2.wireOp",EDGE,"E3.sketch_text.stroke-87")])]});
            var Q7;
            Q7=makeQuery(id+"F3.opExtrude","SWEPT_BODY",BODY,{"disambiguationData":[OSD([sQuery(id+"F2.wireOp",EDGE,"E3.sketch_text.stroke-88"),sQuery(id+"F2.wireOp",EDGE,"E3.sketch_text.stroke-89"),sQuery(id+"F2.wireOp",EDGE,"E3.sketch_text.stroke-90"),sQuery(id+"F2.wireOp",EDGE,"E3.sketch_text.stroke-91")])]});
            var Q8;
            Q8=makeQuery(id+"F3.opExtrude","SWEPT_BODY",BODY,{"disambiguationData":[OSD([sQuery(id+"F2.wireOp",EDGE,"E3.sketch_text.stroke-92"),sQuery(id+"F2.wireOp",EDGE,"E3.sketch_text.stroke-93"),sQuery(id+"F2.wireOp",EDGE,"E3.sketch_text.stroke-94"),sQuery(id+"F2.wireOp",EDGE,"E3.sketch_text.stroke-95"),sQuery(id+"F2.wireOp",EDGE,"E3.sketch_text.stroke-96"),sQuery(id+"F2.wireOp",EDGE,"E3.sketch_text.stroke-97"),sQuery(id+"F2.wireOp",EDGE,"E3.sketch_text.stroke-98"),sQuery(id+"F2.wireOp",EDGE,"E3.sketch_text.stroke-99"),sQuery(id+"F2.wireOp",EDGE,"E3.sketch_text.stroke-100"),sQuery(id+"F2.wireOp",EDGE,"E3.sketch_text.stroke-101"),sQuery(id+"F2.wireOp",EDGE,"E3.sketch_text.stroke-102"),sQuery(id+"F2.wireOp",EDGE,"E3.sketch_text.stroke-103"),sQuery(id+"F2.wireOp",EDGE,"E3.sketch_text.stroke-104"),sQuery(id+"F2.wireOp",EDGE,"E3.sketch_text.stroke-105"),sQuery(id+"F2.wireOp",EDGE,"E3.sketch_text.stroke-106"),sQuery(id+"F2.wireOp",EDGE,"E3.sketch_text.stroke-107"),sQuery(id+"F2.wireOp",EDGE,"E3.sketch_text.stroke-108"),sQuery(id+"F2.wireOp",EDGE,"E3.sketch_text.stroke-109"),sQuery(id+"F2.wireOp",EDGE,"E3.sketch_text.stroke-110"),sQuery(id+"F2.wireOp",EDGE,"E3.sketch_text.stroke-111")])]});
            var Q9;
            Q9=makeQuery(id+"F3.opExtrude","SWEPT_BODY",BODY,{"disambiguationData":[OSD([sQuery(id+"F2.wireOp",EDGE,"E3.sketch_text.stroke-112"),sQuery(id+"F2.wireOp",EDGE,"E3.sketch_text.stroke-113"),sQuery(id+"F2.wireOp",EDGE,"E3.sketch_text.stroke-114"),sQuery(id+"F2.wireOp",EDGE,"E3.sketch_text.stroke-115"),sQuery(id+"F2.wireOp",EDGE,"E3.sketch_text.stroke-116"),sQuery(id+"F2.wireOp",EDGE,"E3.sketch_text.stroke-117"),sQuery(id+"F2.wireOp",EDGE,"E3.sketch_text.stroke-118"),sQuery(id+"F2.wireOp",EDGE,"E3.sketch_text.stroke-119"),sQuery(id+"F2.wireOp",EDGE,"E3.sketch_text.stroke-120"),sQuery(id+"F2.wireOp",EDGE,"E3.sketch_text.stroke-121"),sQuery(id+"F2.wireOp",EDGE,"E3.sketch_text.stroke-122"),sQuery(id+"F2.wireOp",EDGE,"E3.sketch_text.stroke-123"),sQuery(id+"F2.wireOp",EDGE,"E3.sketch_text.stroke-124"),sQuery(id+"F2.wireOp",EDGE,"E3.sketch_text.stroke-125"),sQuery(id+"F2.wireOp",EDGE,"E3.sketch_text.stroke-126"),sQuery(id+"F2.wireOp",EDGE,"E3.sketch_text.stroke-127"),sQuery(id+"F2.wireOp",EDGE,"E3.sketch_text.stroke-128"),sQuery(id+"F2.wireOp",EDGE,"E3.sketch_text.stroke-129")])]});
            var Q10;
            Q10=makeQuery(id+"F3.opExtrude","SWEPT_BODY",BODY,{"disambiguationData":[OSD([sQuery(id+"F2.wireOp",EDGE,"E3.sketch_text.stroke-130"),sQuery(id+"F2.wireOp",EDGE,"E3.sketch_text.stroke-131"),sQuery(id+"F2.wireOp",EDGE,"E3.sketch_text.stroke-132"),sQuery(id+"F2.wireOp",EDGE,"E3.sketch_text.stroke-133"),sQuery(id+"F2.wireOp",EDGE,"E3.sketch_text.stroke-134"),sQuery(id+"F2.wireOp",EDGE,"E3.sketch_text.stroke-135"),sQuery(id+"F2.wireOp",EDGE,"E3.sketch_text.stroke-136"),sQuery(id+"F2.wireOp",EDGE,"E3.sketch_text.stroke-137"),sQuery(id+"F2.wireOp",EDGE,"E3.sketch_text.stroke-138"),sQuery(id+"F2.wireOp",EDGE,"E3.sketch_text.stroke-139"),sQuery(id+"F2.wireOp",EDGE,"E3.sketch_text.stroke-140"),sQuery(id+"F2.wireOp",EDGE,"E3.sketch_text.stroke-141"),sQuery(id+"F2.wireOp",EDGE,"E3.sketch_text.stroke-142"),sQuery(id+"F2.wireOp",EDGE,"E3.sketch_text.stroke-143"),sQuery(id+"F2.wireOp",EDGE,"E3.sketch_text.stroke-144"),sQuery(id+"F2.wireOp",EDGE,"E3.sketch_text.stroke-145"),sQuery(id+"F2.wireOp",EDGE,"E3.sketch_text.stroke-146"),sQuery(id+"F2.wireOp",EDGE,"E3.sketch_text.stroke-147"),sQuery(id+"F2.wireOp",EDGE,"E3.sketch_text.stroke-148"),sQuery(id+"F2.wireOp",EDGE,"E3.sketch_text.stroke-149"),sQuery(id+"F2.wireOp",EDGE,"E3.sketch_text.stroke-150"),sQuery(id+"F2.wireOp",EDGE,"E3.sketch_text.stroke-151"),sQuery(id+"F2.wireOp",EDGE,"E3.sketch_text.stroke-152"),sQuery(id+"F2.wireOp",EDGE,"E3.sketch_text.stroke-153"),sQuery(id+"F2.wireOp",EDGE,"E3.sketch_text.stroke-154"),sQuery(id+"F2.wireOp",EDGE,"E3.sketch_text.stroke-155"),sQuery(id+"F2.wireOp",EDGE,"E3.sketch_text.stroke-156"),sQuery(id+"F2.wireOp",EDGE,"E3.sketch_text.stroke-157")])]});
            var Q11;
            Q11=makeQuery(id+"F3.opExtrude","SWEPT_BODY",BODY,{"disambiguationData":[OSD([sQuery(id+"F2.wireOp",EDGE,"E3.sketch_text.stroke-158"),sQuery(id+"F2.wireOp",EDGE,"E3.sketch_text.stroke-159"),sQuery(id+"F2.wireOp",EDGE,"E3.sketch_text.stroke-160"),sQuery(id+"F2.wireOp",EDGE,"E3.sketch_text.stroke-161"),sQuery(id+"F2.wireOp",EDGE,"E3.sketch_text.stroke-162"),sQuery(id+"F2.wireOp",EDGE,"E3.sketch_text.stroke-163"),sQuery(id+"F2.wireOp",EDGE,"E3.sketch_text.stroke-164"),sQuery(id+"F2.wireOp",EDGE,"E3.sketch_text.stroke-165"),sQuery(id+"F2.wireOp",EDGE,"E3.sketch_text.stroke-166"),sQuery(id+"F2.wireOp",EDGE,"E3.sketch_text.stroke-167"),sQuery(id+"F2.wireOp",EDGE,"E3.sketch_text.stroke-168"),sQuery(id+"F2.wireOp",EDGE,"E3.sketch_text.stroke-169"),sQuery(id+"F2.wireOp",EDGE,"E3.sketch_text.stroke-170"),sQuery(id+"F2.wireOp",EDGE,"E3.sketch_text.stroke-171"),sQuery(id+"F2.wireOp",EDGE,"E3.sketch_text.stroke-172"),sQuery(id+"F2.wireOp",EDGE,"E3.sketch_text.stroke-173"),sQuery(id+"F2.wireOp",EDGE,"E3.sketch_text.stroke-174"),sQuery(id+"F2.wireOp",EDGE,"E3.sketch_text.stroke-175"),sQuery(id+"F2.wireOp",EDGE,"E3.sketch_text.stroke-176"),sQuery(id+"F2.wireOp",EDGE,"E3.sketch_text.stroke-177")])]});
            var Q12;
            Q12=makeQuery(id+"F3.opExtrude","SWEPT_BODY",BODY,{"disambiguationData":[OSD([sQuery(id+"F2.wireOp",EDGE,"E3.sketch_text.stroke-178"),sQuery(id+"F2.wireOp",EDGE,"E3.sketch_text.stroke-179"),sQuery(id+"F2.wireOp",EDGE,"E3.sketch_text.stroke-180"),sQuery(id+"F2.wireOp",EDGE,"E3.sketch_text.stroke-181"),sQuery(id+"F2.wireOp",EDGE,"E3.sketch_text.stroke-182"),sQuery(id+"F2.wireOp",EDGE,"E3.sketch_text.stroke-183"),sQuery(id+"F2.wireOp",EDGE,"E3.sketch_text.stroke-184"),sQuery(id+"F2.wireOp",EDGE,"E3.sketch_text.stroke-185"),sQuery(id+"F2.wireOp",EDGE,"E3.sketch_text.stroke-186"),sQuery(id+"F2.wireOp",EDGE,"E3.sketch_text.stroke-187"),sQuery(id+"F2.wireOp",EDGE,"E3.sketch_text.stroke-188"),sQuery(id+"F2.wireOp",EDGE,"E3.sketch_text.stroke-189"),sQuery(id+"F2.wireOp",EDGE,"E3.sketch_text.stroke-190"),sQuery(id+"F2.wireOp",EDGE,"E3.sketch_text.stroke-191"),sQuery(id+"F2.wireOp",EDGE,"E3.sketch_text.stroke-192"),sQuery(id+"F2.wireOp",EDGE,"E3.sketch_text.stroke-193"),sQuery(id+"F2.wireOp",EDGE,"E3.sketch_text.stroke-194"),sQuery(id+"F2.wireOp",EDGE,"E3.sketch_text.stroke-195")])]});
            transform(context, id + "F9", {"entities" : qUnion([Q0, Q1, Q2, Q3, Q4, Q5, Q6, Q7, Q8, Q9, Q10, Q11, Q12]), "transformType" : TransformType.TRANSLATION_3D, "dx" : 0 * mm, "dy" : 0 * mm, "dz" : -1.3 * mm, "makeCopy" : false});
        }
        {
            var Q0;
            Q0=makeQuery(id+"F3.opExtrude","SWEPT_BODY",BODY,{"disambiguationData":[OSD([sQuery(id+"F2.wireOp",EDGE,"E3.sketch_text.stroke-0"),sQuery(id+"F2.wireOp",EDGE,"E3.sketch_text.stroke-1"),sQuery(id+"F2.wireOp",EDGE,"E3.sketch_text.stroke-2"),sQuery(id+"F2.wireOp",EDGE,"E3.sketch_text.stroke-3"),sQuery(id+"F2.wireOp",EDGE,"E3.sketch_text.stroke-4"),sQuery(id+"F2.wireOp",EDGE,"E3.sketch_text.stroke-5"),sQuery(id+"F2.wireOp",EDGE,"E3.sketch_text.stroke-6"),sQuery(id+"F2.wireOp",EDGE,"E3.sketch_text.stroke-7"),sQuery(id+"F2.wireOp",EDGE,"E3.sketch_text.stroke-8"),sQuery(id+"F2.wireOp",EDGE,"E3.sketch_text.stroke-9"),sQuery(id+"F2.wireOp",EDGE,"E3.sketch_text.stroke-10"),sQuery(id+"F2.wireOp",EDGE,"E3.sketch_text.stroke-11")])]});
            var Q1;
            Q1=makeQuery(id+"F3.opExtrude","SWEPT_BODY",BODY,{"disambiguationData":[OSD([sQuery(id+"F2.wireOp",EDGE,"E3.sketch_text.stroke-12"),sQuery(id+"F2.wireOp",EDGE,"E3.sketch_text.stroke-13"),sQuery(id+"F2.wireOp",EDGE,"E3.sketch_text.stroke-14"),sQuery(id+"F2.wireOp",EDGE,"E3.sketch_text.stroke-15"),sQuery(id+"F2.wireOp",EDGE,"E3.sketch_text.stroke-16"),sQuery(id+"F2.wireOp",EDGE,"E3.sketch_text.stroke-17"),sQuery(id+"F2.wireOp",EDGE,"E3.sketch_text.stroke-18"),sQuery(id+"F2.wireOp",EDGE,"E3.sketch_text.stroke-19"),sQuery(id+"F2.wireOp",EDGE,"E3.sketch_text.stroke-20"),sQuery(id+"F2.wireOp",EDGE,"E3.sketch_text.stroke-21"),sQuery(id+"F2.wireOp",EDGE,"E3.sketch_text.stroke-22"),sQuery(id+"F2.wireOp",EDGE,"E3.sketch_text.stroke-23"),sQuery(id+"F2.wireOp",EDGE,"E3.sketch_text.stroke-24"),sQuery(id+"F2.wireOp",EDGE,"E3.sketch_text.stroke-25"),sQuery(id+"F2.wireOp",EDGE,"E3.sketch_text.stroke-26"),sQuery(id+"F2.wireOp",EDGE,"E3.sketch_text.stroke-27"),sQuery(id+"F2.wireOp",EDGE,"E3.sketch_text.stroke-28"),sQuery(id+"F2.wireOp",EDGE,"E3.sketch_text.stroke-29"),sQuery(id+"F2.wireOp",EDGE,"E3.sketch_text.stroke-30")])]});
            var Q2;
            Q2=makeQuery(id+"F3.opExtrude","SWEPT_BODY",BODY,{"disambiguationData":[OSD([sQuery(id+"F2.wireOp",EDGE,"E3.sketch_text.stroke-31"),sQuery(id+"F2.wireOp",EDGE,"E3.sketch_text.stroke-32"),sQuery(id+"F2.wireOp",EDGE,"E3.sketch_text.stroke-33"),sQuery(id+"F2.wireOp",EDGE,"E3.sketch_text.stroke-34"),sQuery(id+"F2.wireOp",EDGE,"E3.sketch_text.stroke-35"),sQuery(id+"F2.wireOp",EDGE,"E3.sketch_text.stroke-36"),sQuery(id+"F2.wireOp",EDGE,"E3.sketch_text.stroke-37"),sQuery(id+"F2.wireOp",EDGE,"E3.sketch_text.stroke-38"),sQuery(id+"F2.wireOp",EDGE,"E3.sketch_text.stroke-39"),sQuery(id+"F2.wireOp",EDGE,"E3.sketch_text.stroke-40")])]});
            var Q3;
            Q3=makeQuery(id+"F3.opExtrude","SWEPT_BODY",BODY,{"disambiguationData":[OSD([sQuery(id+"F2.wireOp",EDGE,"E3.sketch_text.stroke-41"),sQuery(id+"F2.wireOp",EDGE,"E3.sketch_text.stroke-42"),sQuery(id+"F2.wireOp",EDGE,"E3.sketch_text.stroke-43"),sQuery(id+"F2.wireOp",EDGE,"E3.sketch_text.stroke-44"),sQuery(id+"F2.wireOp",EDGE,"E3.sketch_text.stroke-45"),sQuery(id+"F2.wireOp",EDGE,"E3.sketch_text.stroke-46"),sQuery(id+"F2.wireOp",EDGE,"E3.sketch_text.stroke-47"),sQuery(id+"F2.wireOp",EDGE,"E3.sketch_text.stroke-48"),sQuery(id+"F2.wireOp",EDGE,"E3.sketch_text.stroke-49"),sQuery(id+"F2.wireOp",EDGE,"E3.sketch_text.stroke-50")])]});
            var Q4;
            Q4=makeQuery(id+"F3.opExtrude","SWEPT_BODY",BODY,{"disambiguationData":[OSD([sQuery(id+"F2.wireOp",EDGE,"E3.sketch_text.stroke-51"),sQuery(id+"F2.wireOp",EDGE,"E3.sketch_text.stroke-52"),sQuery(id+"F2.wireOp",EDGE,"E3.sketch_text.stroke-53"),sQuery(id+"F2.wireOp",EDGE,"E3.sketch_text.stroke-54"),sQuery(id+"F2.wireOp",EDGE,"E3.sketch_text.stroke-55"),sQuery(id+"F2.wireOp",EDGE,"E3.sketch_text.stroke-56"),sQuery(id+"F2.wireOp",EDGE,"E3.sketch_text.stroke-57"),sQuery(id+"F2.wireOp",EDGE,"E3.sketch_text.stroke-58"),sQuery(id+"F2.wireOp",EDGE,"E3.sketch_text.stroke-59"),sQuery(id+"F2.wireOp",EDGE,"E3.sketch_text.stroke-60"),sQuery(id+"F2.wireOp",EDGE,"E3.sketch_text.stroke-61"),sQuery(id+"F2.wireOp",EDGE,"E3.sketch_text.stroke-62"),sQuery(id+"F2.wireOp",EDGE,"E3.sketch_text.stroke-63"),sQuery(id+"F2.wireOp",EDGE,"E3.sketch_text.stroke-64"),sQuery(id+"F2.wireOp",EDGE,"E3.sketch_text.stroke-65")])]});
            var Q5;
            Q5=makeQuery(id+"F3.opExtrude","SWEPT_BODY",BODY,{"disambiguationData":[OSD([sQuery(id+"F2.wireOp",EDGE,"E3.sketch_text.stroke-66"),sQuery(id+"F2.wireOp",EDGE,"E3.sketch_text.stroke-67"),sQuery(id+"F2.wireOp",EDGE,"E3.sketch_text.stroke-68"),sQuery(id+"F2.wireOp",EDGE,"E3.sketch_text.stroke-69"),sQuery(id+"F2.wireOp",EDGE,"E3.sketch_text.stroke-70"),sQuery(id+"F2.wireOp",EDGE,"E3.sketch_text.stroke-71"),sQuery(id+"F2.wireOp",EDGE,"E3.sketch_text.stroke-72"),sQuery(id+"F2.wireOp",EDGE,"E3.sketch_text.stroke-73"),sQuery(id+"F2.wireOp",EDGE,"E3.sketch_text.stroke-74"),sQuery(id+"F2.wireOp",EDGE,"E3.sketch_text.stroke-75"),sQuery(id+"F2.wireOp",EDGE,"E3.sketch_text.stroke-76"),sQuery(id+"F2.wireOp",EDGE,"E3.sketch_text.stroke-77"),sQuery(id+"F2.wireOp",EDGE,"E3.sketch_text.stroke-78"),sQuery(id+"F2.wireOp",EDGE,"E3.sketch_text.stroke-79"),sQuery(id+"F2.wireOp",EDGE,"E3.sketch_text.stroke-80"),sQuery(id+"F2.wireOp",EDGE,"E3.sketch_text.stroke-81"),sQuery(id+"F2.wireOp",EDGE,"E3.sketch_text.stroke-82"),sQuery(id+"F2.wireOp",EDGE,"E3.sketch_text.stroke-83")])]});
            var Q6;
            Q6=makeQuery(id+"F3.opExtrude","SWEPT_BODY",BODY,{"disambiguationData":[OSD([sQuery(id+"F2.wireOp",EDGE,"E3.sketch_text.stroke-84"),sQuery(id+"F2.wireOp",EDGE,"E3.sketch_text.stroke-85"),sQuery(id+"F2.wireOp",EDGE,"E3.sketch_text.stroke-86"),sQuery(id+"F2.wireOp",EDGE,"E3.sketch_text.stroke-87")])]});
            var Q7;
            Q7=makeQuery(id+"F3.opExtrude","SWEPT_BODY",BODY,{"disambiguationData":[OSD([sQuery(id+"F2.wireOp",EDGE,"E3.sketch_text.stroke-92"),sQuery(id+"F2.wireOp",EDGE,"E3.sketch_text.stroke-93"),sQuery(id+"F2.wireOp",EDGE,"E3.sketch_text.stroke-94"),sQuery(id+"F2.wireOp",EDGE,"E3.sketch_text.stroke-95"),sQuery(id+"F2.wireOp",EDGE,"E3.sketch_text.stroke-96"),sQuery(id+"F2.wireOp",EDGE,"E3.sketch_text.stroke-97"),sQuery(id+"F2.wireOp",EDGE,"E3.sketch_text.stroke-98"),sQuery(id+"F2.wireOp",EDGE,"E3.sketch_text.stroke-99"),sQuery(id+"F2.wireOp",EDGE,"E3.sketch_text.stroke-100"),sQuery(id+"F2.wireOp",EDGE,"E3.sketch_text.stroke-101"),sQuery(id+"F2.wireOp",EDGE,"E3.sketch_text.stroke-102"),sQuery(id+"F2.wireOp",EDGE,"E3.sketch_text.stroke-103"),sQuery(id+"F2.wireOp",EDGE,"E3.sketch_text.stroke-104"),sQuery(id+"F2.wireOp",EDGE,"E3.sketch_text.stroke-105"),sQuery(id+"F2.wireOp",EDGE,"E3.sketch_text.stroke-106"),sQuery(id+"F2.wireOp",EDGE,"E3.sketch_text.stroke-107"),sQuery(id+"F2.wireOp",EDGE,"E3.sketch_text.stroke-108"),sQuery(id+"F2.wireOp",EDGE,"E3.sketch_text.stroke-109"),sQuery(id+"F2.wireOp",EDGE,"E3.sketch_text.stroke-110"),sQuery(id+"F2.wireOp",EDGE,"E3.sketch_text.stroke-111")])]});
            var Q8;
            Q8=makeQuery(id+"F3.opExtrude","SWEPT_BODY",BODY,{"disambiguationData":[OSD([sQuery(id+"F2.wireOp",EDGE,"E3.sketch_text.stroke-88"),sQuery(id+"F2.wireOp",EDGE,"E3.sketch_text.stroke-89"),sQuery(id+"F2.wireOp",EDGE,"E3.sketch_text.stroke-90"),sQuery(id+"F2.wireOp",EDGE,"E3.sketch_text.stroke-91")])]});
            var Q9;
            Q9=makeQuery(id+"F3.opExtrude","SWEPT_BODY",BODY,{"disambiguationData":[OSD([sQuery(id+"F2.wireOp",EDGE,"E3.sketch_text.stroke-112"),sQuery(id+"F2.wireOp",EDGE,"E3.sketch_text.stroke-113"),sQuery(id+"F2.wireOp",EDGE,"E3.sketch_text.stroke-114"),sQuery(id+"F2.wireOp",EDGE,"E3.sketch_text.stroke-115"),sQuery(id+"F2.wireOp",EDGE,"E3.sketch_text.stroke-116"),sQuery(id+"F2.wireOp",EDGE,"E3.sketch_text.stroke-117"),sQuery(id+"F2.wireOp",EDGE,"E3.sketch_text.stroke-118"),sQuery(id+"F2.wireOp",EDGE,"E3.sketch_text.stroke-119"),sQuery(id+"F2.wireOp",EDGE,"E3.sketch_text.stroke-120"),sQuery(id+"F2.wireOp",EDGE,"E3.sketch_text.stroke-121"),sQuery(id+"F2.wireOp",EDGE,"E3.sketch_text.stroke-122"),sQuery(id+"F2.wireOp",EDGE,"E3.sketch_text.stroke-123"),sQuery(id+"F2.wireOp",EDGE,"E3.sketch_text.stroke-124"),sQuery(id+"F2.wireOp",EDGE,"E3.sketch_text.stroke-125"),sQuery(id+"F2.wireOp",EDGE,"E3.sketch_text.stroke-126"),sQuery(id+"F2.wireOp",EDGE,"E3.sketch_text.stroke-127"),sQuery(id+"F2.wireOp",EDGE,"E3.sketch_text.stroke-128"),sQuery(id+"F2.wireOp",EDGE,"E3.sketch_text.stroke-129")])]});
            var Q10;
            Q10=makeQuery(id+"F3.opExtrude","SWEPT_BODY",BODY,{"disambiguationData":[OSD([sQuery(id+"F2.wireOp",EDGE,"E3.sketch_text.stroke-130"),sQuery(id+"F2.wireOp",EDGE,"E3.sketch_text.stroke-131"),sQuery(id+"F2.wireOp",EDGE,"E3.sketch_text.stroke-132"),sQuery(id+"F2.wireOp",EDGE,"E3.sketch_text.stroke-133"),sQuery(id+"F2.wireOp",EDGE,"E3.sketch_text.stroke-134"),sQuery(id+"F2.wireOp",EDGE,"E3.sketch_text.stroke-135"),sQuery(id+"F2.wireOp",EDGE,"E3.sketch_text.stroke-136"),sQuery(id+"F2.wireOp",EDGE,"E3.sketch_text.stroke-137"),sQuery(id+"F2.wireOp",EDGE,"E3.sketch_text.stroke-138"),sQuery(id+"F2.wireOp",EDGE,"E3.sketch_text.stroke-139"),sQuery(id+"F2.wireOp",EDGE,"E3.sketch_text.stroke-140"),sQuery(id+"F2.wireOp",EDGE,"E3.sketch_text.stroke-141"),sQuery(id+"F2.wireOp",EDGE,"E3.sketch_text.stroke-142"),sQuery(id+"F2.wireOp",EDGE,"E3.sketch_text.stroke-143"),sQuery(id+"F2.wireOp",EDGE,"E3.sketch_text.stroke-144"),sQuery(id+"F2.wireOp",EDGE,"E3.sketch_text.stroke-145"),sQuery(id+"F2.wireOp",EDGE,"E3.sketch_text.stroke-146"),sQuery(id+"F2.wireOp",EDGE,"E3.sketch_text.stroke-147"),sQuery(id+"F2.wireOp",EDGE,"E3.sketch_text.stroke-148"),sQuery(id+"F2.wireOp",EDGE,"E3.sketch_text.stroke-149"),sQuery(id+"F2.wireOp",EDGE,"E3.sketch_text.stroke-150"),sQuery(id+"F2.wireOp",EDGE,"E3.sketch_text.stroke-151"),sQuery(id+"F2.wireOp",EDGE,"E3.sketch_text.stroke-152"),sQuery(id+"F2.wireOp",EDGE,"E3.sketch_text.stroke-153"),sQuery(id+"F2.wireOp",EDGE,"E3.sketch_text.stroke-154"),sQuery(id+"F2.wireOp",EDGE,"E3.sketch_text.stroke-155"),sQuery(id+"F2.wireOp",EDGE,"E3.sketch_text.stroke-156"),sQuery(id+"F2.wireOp",EDGE,"E3.sketch_text.stroke-157")])]});
            var Q11;
            Q11=makeQuery(id+"F3.opExtrude","SWEPT_BODY",BODY,{"disambiguationData":[OSD([sQuery(id+"F2.wireOp",EDGE,"E3.sketch_text.stroke-158"),sQuery(id+"F2.wireOp",EDGE,"E3.sketch_text.stroke-159"),sQuery(id+"F2.wireOp",EDGE,"E3.sketch_text.stroke-160"),sQuery(id+"F2.wireOp",EDGE,"E3.sketch_text.stroke-161"),sQuery(id+"F2.wireOp",EDGE,"E3.sketch_text.stroke-162"),sQuery(id+"F2.wireOp",EDGE,"E3.sketch_text.stroke-163"),sQuery(id+"F2.wireOp",EDGE,"E3.sketch_text.stroke-164"),sQuery(id+"F2.wireOp",EDGE,"E3.sketch_text.stroke-165"),sQuery(id+"F2.wireOp",EDGE,"E3.sketch_text.stroke-166"),sQuery(id+"F2.wireOp",EDGE,"E3.sketch_text.stroke-167"),sQuery(id+"F2.wireOp",EDGE,"E3.sketch_text.stroke-168"),sQuery(id+"F2.wireOp",EDGE,"E3.sketch_text.stroke-169"),sQuery(id+"F2.wireOp",EDGE,"E3.sketch_text.stroke-170"),sQuery(id+"F2.wireOp",EDGE,"E3.sketch_text.stroke-171"),sQuery(id+"F2.wireOp",EDGE,"E3.sketch_text.stroke-172"),sQuery(id+"F2.wireOp",EDGE,"E3.sketch_text.stroke-173"),sQuery(id+"F2.wireOp",EDGE,"E3.sketch_text.stroke-174"),sQuery(id+"F2.wireOp",EDGE,"E3.sketch_text.stroke-175"),sQuery(id+"F2.wireOp",EDGE,"E3.sketch_text.stroke-176"),sQuery(id+"F2.wireOp",EDGE,"E3.sketch_text.stroke-177")])]});
            var Q12;
            Q12=makeQuery(id+"F3.opExtrude","SWEPT_BODY",BODY,{"disambiguationData":[OSD([sQuery(id+"F2.wireOp",EDGE,"E3.sketch_text.stroke-178"),sQuery(id+"F2.wireOp",EDGE,"E3.sketch_text.stroke-179"),sQuery(id+"F2.wireOp",EDGE,"E3.sketch_text.stroke-180"),sQuery(id+"F2.wireOp",EDGE,"E3.sketch_text.stroke-181"),sQuery(id+"F2.wireOp",EDGE,"E3.sketch_text.stroke-182"),sQuery(id+"F2.wireOp",EDGE,"E3.sketch_text.stroke-183"),sQuery(id+"F2.wireOp",EDGE,"E3.sketch_text.stroke-184"),sQuery(id+"F2.wireOp",EDGE,"E3.sketch_text.stroke-185"),sQuery(id+"F2.wireOp",EDGE,"E3.sketch_text.stroke-186"),sQuery(id+"F2.wireOp",EDGE,"E3.sketch_text.stroke-187"),sQuery(id+"F2.wireOp",EDGE,"E3.sketch_text.stroke-188"),sQuery(id+"F2.wireOp",EDGE,"E3.sketch_text.stroke-189"),sQuery(id+"F2.wireOp",EDGE,"E3.sketch_text.stroke-190"),sQuery(id+"F2.wireOp",EDGE,"E3.sketch_text.stroke-191"),sQuery(id+"F2.wireOp",EDGE,"E3.sketch_text.stroke-192"),sQuery(id+"F2.wireOp",EDGE,"E3.sketch_text.stroke-193"),sQuery(id+"F2.wireOp",EDGE,"E3.sketch_text.stroke-194"),sQuery(id+"F2.wireOp",EDGE,"E3.sketch_text.stroke-195")])]});
            var Q13;
            Q13=makeQuery(id+"F1.opExtrude","SWEPT_BODY",BODY,{"disambiguationData":[OSD([sQuery(id+"F0.wireOp",EDGE,"E0.bottom"),sQuery(id+"F0.wireOp",EDGE,"E0.top"),sQuery(id+"F0.wireOp",EDGE,"E0.left"),sQuery(id+"F0.wireOp",EDGE,"E0.right"),sQuery(id+"F0.wireOp",EDGE,"E1.bottom"),sQuery(id+"F0.wireOp",EDGE,"E1.top"),sQuery(id+"F0.wireOp",EDGE,"E1.left"),sQuery(id+"F0.wireOp",EDGE,"E1.right")])]});
            booleanBodies(context, id + "F10", {"operationType" : BooleanOperationType.SUBTRACTION, "tools" : qUnion([Q0, Q1, Q2, Q3, Q4, Q5, Q6, Q7, Q8, Q9, Q10, Q11, Q12]), "targets" : qUnion([Q13])});
        }
    });
